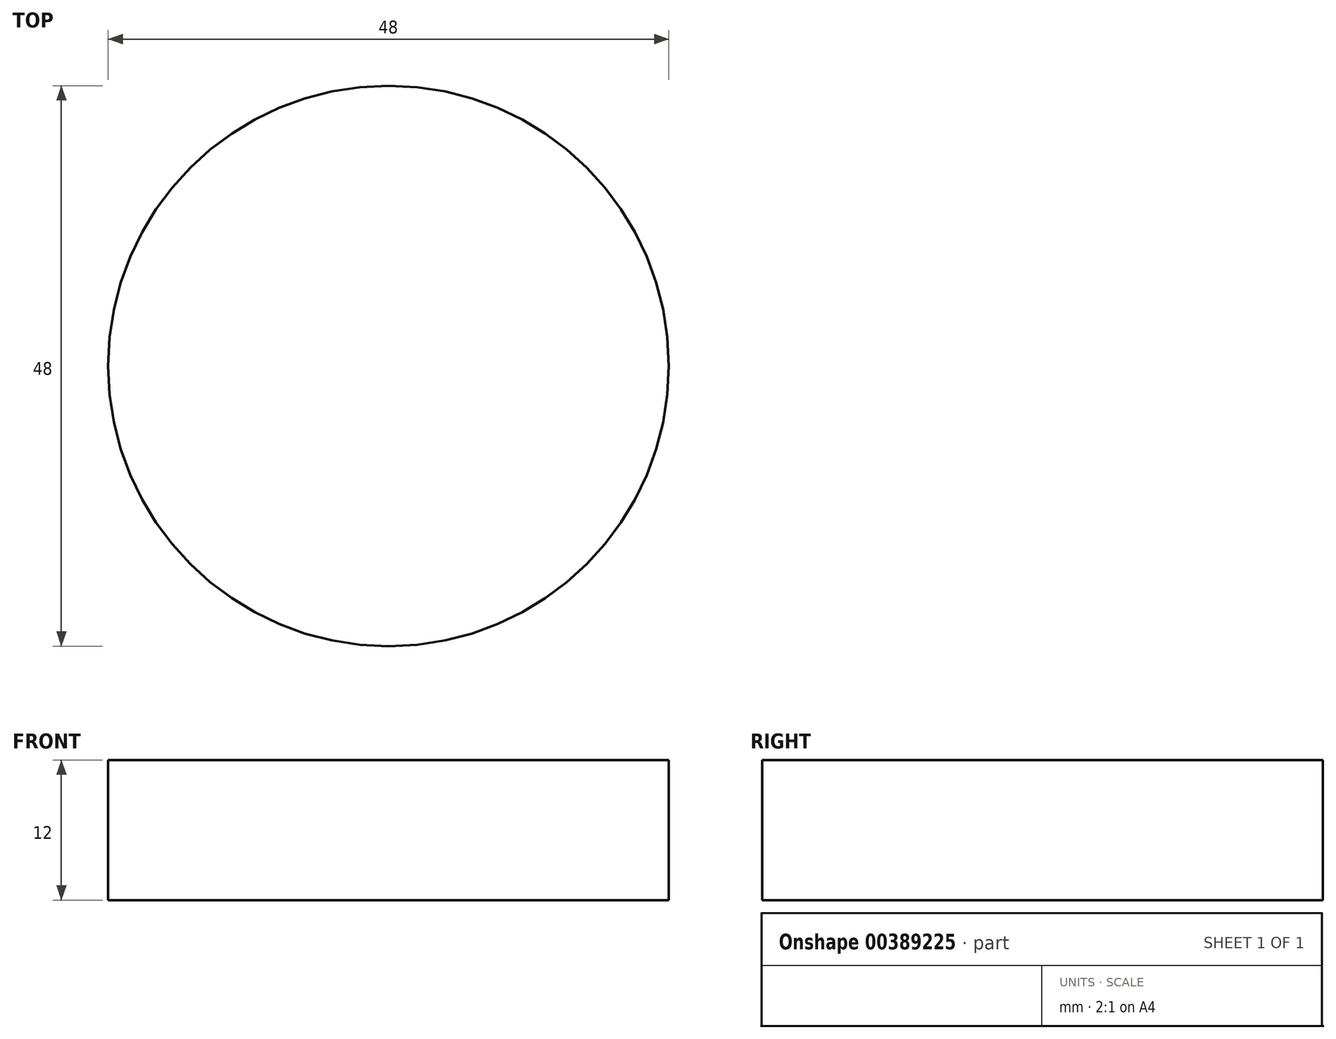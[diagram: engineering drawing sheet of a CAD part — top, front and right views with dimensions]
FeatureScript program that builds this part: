
annotation { "Feature Type Name" : "Feature", "Feature Type Description" : "" }
export const myFeature = defineFeature(function(context is Context, id is Id, definition is map)
    precondition{}
    {
        {
            var Q0;
            Q0=qCreatedBy(makeId("Top.planeOp"),FACE);
            var sketch = newSketch(context, id + "F0", { "sketchPlane" : qUnion([Q0])});
            skCircle(sketch, "E0", {"center": v(0, 0) * mm, "radius": 24 * mm});
            skSolve(sketch);
        }
        {
            var Q0;
            Q0=makeQuery(id+"F0.imprint","IMPRINT",FACE,{"disambiguationData":[TD([[makeQuery(id+"F0.imprint","IMPRINT",EDGE,{"derivedFrom":sQuery(id+"F0.wireOp",EDGE,"E0")}),1.0]])]});
            extrude(context, id + "F1", {"entities" : qUnion([Q0]), "depth" : 12 * mm});
        }
    });
